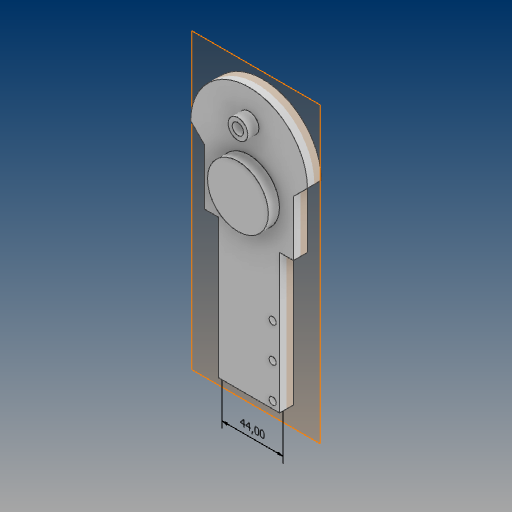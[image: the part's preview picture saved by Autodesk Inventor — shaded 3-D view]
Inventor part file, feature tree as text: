
AUTODESK INVENTOR PART (.ipt)
format: ipt  version: 2021 (Build 250183000, 183)  size: 187,904 bytes
history: native  units: mm
features: other x6, sketch x5, extrude x4, reference x4, projected_geometry x4, plane x1, mirror x1, hole x1
ambient origin geometry x8: Origin, YZ Plane, XZ Plane, XY Plane, X Axis, Y Axis, Z Axis, Center Point
bodies: Solid1 (feature_tree)
feature tree (26):
  other  "Annotations"
  extrude  "Extrusion1"  Depth=7.2mm
  extrude  "Extrusion2"  Depth=43.8mm
  extrude  "Extrusion3"  Depth=42.0mm
  extrude  "Extrusion4"  Depth=8.0mm TaperAngle=0.0deg
  plane  "Work Plane1"
  mirror  "Mirror1"
  hole  "Hole1"  [1 undecoded]
  sketch  "Sketch1"  dims[d0=14.2mm d1=7.2mm]
  reference  "Reference1"
  sketch  "Sketch2"  dims[d2=27.0mm d3=43.8mm]
  projected_geometry  "Projected Loop1"
  projected_geometry  "Projected Loop2"
  sketch  "Sketch3"  dims[d4=42.0mm d5=150.0mm]
  projected_geometry  "Projected Loop3"
  sketch  "Sketch4"  dims[d6=20.0mm d7=8.0mm d8=0.0mm]
  projected_geometry  "Projected Loop4"
  sketch  "Sketch5"  dims[d9=10.0mm d10=0.0mm d11=8.2mm d12=6.0mm d13=4.0mm d14=2.0mm d15=90.0deg d16=8.0mm d17=20.594885mm d18=10.0mm d19=135.0deg d20=10.0mm d21=0.0mm d22=10.0mm d23=100.0mm d27=0.0mm d28=0.0mm d24=0.49838mm d25=7.520724mm d26=44.0mm d29=0.5mm d30=0.872665mm d31=0.5mm d32=0.872665mm]
  reference  "Reference2"
  reference  "Reference3"
  reference  "Reference4"
  other  "<userpath>\Desktop\DO_AN_TOT_NGHIEP_2024\Mechanical\Design_in_3D\Version_1\002_Bo_truot.iam"
  other  "002_Bo_truot.iam"
  other  "16_Khau_hai:1"
  other  "18_Kep_han_A:1"
  other  "Linear Dimension 1"
note: 1 required parameter value undecoded (feature->parameter linkage not recoverable at this tier; creation-order binding heuristic only, values carry confidence <= 0.55)
